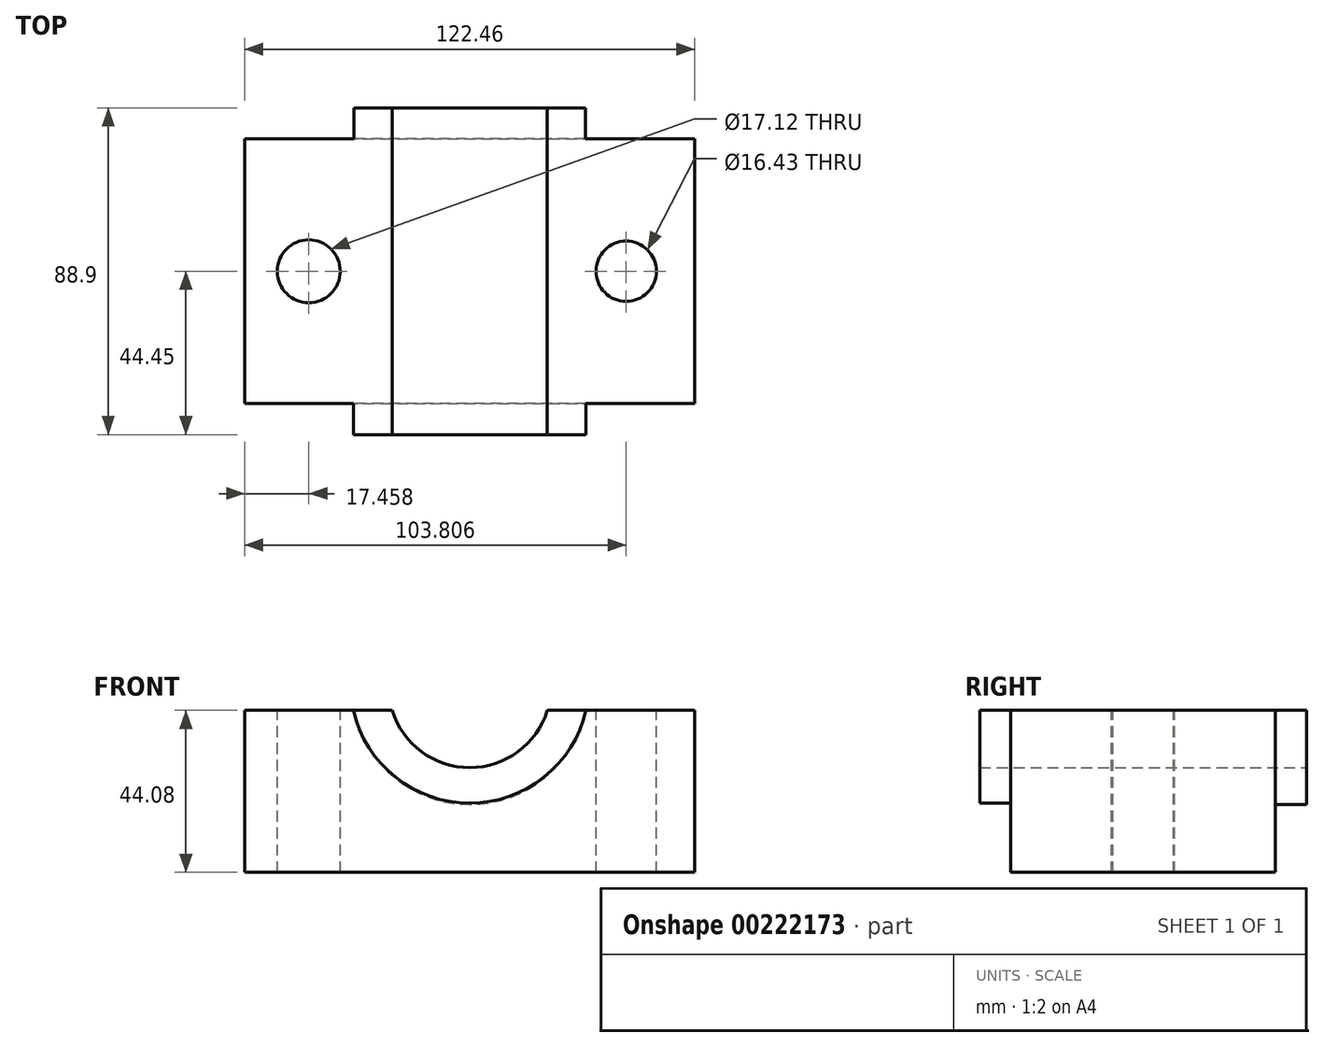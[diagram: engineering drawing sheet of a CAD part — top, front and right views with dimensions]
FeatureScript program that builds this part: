
annotation { "Feature Type Name" : "Feature", "Feature Type Description" : "" }
export const myFeature = defineFeature(function(context is Context, id is Id, definition is map)
    precondition{}
    {
        {
            var Q0;
            Q0=qCreatedBy(makeId("Top.planeOp"),FACE);
            var sketch = newSketch(context, id + "F0", { "sketchPlane" : qUnion([Q0])});
            skLineSegment(sketch, "E0.bottom", {"start": v(-61.23, -36) * mm, "end": v(61.23, -36) * mm});
            skLineSegment(sketch, "E0.top", {"start": v(-61.23, 36) * mm, "end": v(61.23, 36) * mm});
            skLineSegment(sketch, "E0.left", {"start": v(-61.23, -36) * mm, "end": v(-61.23, 36) * mm});
            skLineSegment(sketch, "E0.right", {"start": v(61.23, -36) * mm, "end": v(61.23, 36) * mm});
            skPoint(sketch, "E0.middle", {"position": v(0, 0) * mm});
            skSolve(sketch);
        }
        {
            var Q0;
            Q0 = qSketchRegion(id + "F0", true);
            extrude(context, id + "F1", {"entities" : qUnion([Q0]), "depth" : 76.2 * mm});
        }
        {
            var Q0;
            Q0=qCreatedBy(makeId("Front.planeOp"),FACE);
            var sketch = newSketch(context, id + "F2", { "sketchPlane" : qUnion([Q0])});
            skCircle(sketch, "E1", {"center": v(0, 51.3) * mm, "radius": 32.46 * mm});
            skSolve(sketch);
        }
        {
            var Q0;
            Q0 = qSketchRegion(id + "F2", true);
            extrude(context, id + "F3", {"entities" : qUnion([Q0]), "operationType" : NewBodyOperationType.ADD, "depth" : 44.45 * mm});
        }
        {
            var Q0;
            Q0=qCreatedBy(makeId("Front.planeOp"),FACE);
            var sketch = newSketch(context, id + "F4", { "sketchPlane" : qUnion([Q0])});
            skCircle(sketch, "E2", {"center": v(0, 50.6) * mm, "radius": 32.16 * mm});
            skSolve(sketch);
        }
        {
            var Q0;
            Q0 = qSketchRegion(id + "F4", true);
            extrude(context, id + "F5", {"entities" : qUnion([Q0]), "operationType" : NewBodyOperationType.ADD, "oppositeDirection" : true, "depth" : 44.45 * mm});
        }
        {
            var Q0;
            Q0=makeQuery(id+"F5.opExtrude","CAP_FACE",FACE,{"disambiguationData":[OSD([sQuery(id+"F4.wireOp",EDGE,"E2")])],"isStart":false});
            var sketch = newSketch(context, id + "F6", { "sketchPlane" : qUnion([Q0])});
            skCircle(sketch, "E3", {"center": v(0, 50.6) * mm, "radius": 22.1 * mm});
            skSolve(sketch);
        }
        {
            var Q0;
            Q0 = qSketchRegion(id + "F6", true);
            extrude(context, id + "F7", {"entities" : qUnion([Q0]), "operationType" : NewBodyOperationType.REMOVE, "endBound" : BoundingType.THROUGH_ALL, "oppositeDirection" : true, "depth" : 25.4 * mm});
        }
        {
            var Q0;
            {var subQ0=sQuery(id+"F0.wireOp",EDGE,"E0.left");var subQ2=sQuery(id+"F0.wireOp",EDGE,"E0.top");var subQ3=sQuery(id+"F0.wireOp",EDGE,"E0.bottom");Q0=makeQuery(id+"F5.boolean.opBoolean","SPLIT",FACE,{"disambiguationData":[TD([makeQuery(id+"F1.opExtrude","SWEPT_FACE",FACE,{"disambiguationData":[OSD([subQ0])]})])],"derivedFrom":makeQuery(id+"F1.opExtrude","CAP_FACE",FACE,{"disambiguationData":[OSD([subQ3,subQ2,subQ0,sQuery(id+"F0.wireOp",EDGE,"E0.right")])],"isStart":false})});}
            var sketch = newSketch(context, id + "F8", { "sketchPlane" : qUnion([Q0])});
            skCircle(sketch, "E4", {"center": v(-43.77, 0) * mm, "radius": 8.56 * mm});
            skCircle(sketch, "E5", {"center": v(42.58, 0) * mm, "radius": 8.21 * mm});
            skSolve(sketch);
        }
        {
            var Q0;
            Q0 = qSketchRegion(id + "F8", true);
            extrude(context, id + "F9", {"entities" : qUnion([Q0]), "operationType" : NewBodyOperationType.REMOVE, "endBound" : BoundingType.THROUGH_ALL, "oppositeDirection" : true, "depth" : 25.4 * mm});
        }
        {
            var Q0;
            Q0=makeQuery(id+"F1.opExtrude","SWEPT_FACE",FACE,{"disambiguationData":[OSD([sQuery(id+"F0.wireOp",EDGE,"E0.bottom")])]});
            var sketch = newSketch(context, id + "F10", { "sketchPlane" : qUnion([Q0])});
            skLineSegment(sketch, "E6.bottom", {"start": v(-61.23, 44.08) * mm, "end": v(61.23, 44.08) * mm});
            skLineSegment(sketch, "E6.top", {"start": v(-61.23, 84.5) * mm, "end": v(61.23, 84.5) * mm});
            skLineSegment(sketch, "E6.left", {"start": v(-61.23, 44.08) * mm, "end": v(-61.23, 84.5) * mm});
            skLineSegment(sketch, "E6.right", {"start": v(61.23, 44.08) * mm, "end": v(61.23, 84.5) * mm});
            skSolve(sketch);
        }
        {
            var Q0;
            Q0 = qSketchRegion(id + "F10", true);
            extrude(context, id + "F11", {"entities" : qUnion([Q0]), "operationType" : NewBodyOperationType.REMOVE, "endBound" : BoundingType.THROUGH_ALL, "oppositeDirection" : true, "depth" : 25.4 * mm});
        }
        {
            var Q0;
            Q0=makeQuery(id+"F1.opExtrude","SWEPT_FACE",FACE,{"disambiguationData":[OSD([sQuery(id+"F0.wireOp",EDGE,"E0.bottom")])]});
            var sketch = newSketch(context, id + "F12", { "sketchPlane" : qUnion([Q0])});
            skLineSegment(sketch, "E7.bottom", {"start": v(-61.23, 44.08) * mm, "end": v(61.53, 44.08) * mm});
            skLineSegment(sketch, "E7.top", {"start": v(-61.23, 85.34) * mm, "end": v(61.53, 85.34) * mm});
            skLineSegment(sketch, "E7.left", {"start": v(-61.23, 44.08) * mm, "end": v(-61.23, 85.34) * mm});
            skLineSegment(sketch, "E7.right", {"start": v(61.53, 44.08) * mm, "end": v(61.53, 85.34) * mm});
            skSolve(sketch);
        }
        {
            var Q0;
            Q0 = qSketchRegion(id + "F12", true);
            extrude(context, id + "F13", {"entities" : qUnion([Q0]), "operationType" : NewBodyOperationType.REMOVE, "endBound" : BoundingType.THROUGH_ALL, "oppositeDirection" : true, "depth" : 50.8 * mm});
        }
        {
            var Q0;
            Q0=makeQuery(id+"F11.boolean.opBoolean","COPY",FACE,{"derivedFrom":makeQuery(id+"F11.opExtrude","CAP_FACE",FACE,{"disambiguationData":[OSD([sQuery(id+"F10.wireOp",EDGE,"E6.bottom"),sQuery(id+"F10.wireOp",EDGE,"E6.top"),sQuery(id+"F10.wireOp",EDGE,"E6.left"),sQuery(id+"F10.wireOp",EDGE,"E6.right")])],"isStart":true})});
            var sketch = newSketch(context, id + "F14", { "sketchPlane" : qUnion([Q0])});
            skArc(sketch, "E8", {"start": v(31.65, 44.08) * mm, "mid": v(0, 84.2) * mm, "end": v(-31.65, 44.08) * mm});
            skLineSegment(sketch, "E9", {"start": v(-31.65, 44.08) * mm, "end": v(31.65, 44.08) * mm});
            skSolve(sketch);
        }
        {
            var Q0;
            Q0 = qSketchRegion(id + "F14", true);
            extrude(context, id + "F15", {"entities" : qUnion([Q0]), "operationType" : NewBodyOperationType.REMOVE, "endBound" : BoundingType.THROUGH_ALL, "oppositeDirection" : true, "depth" : 25.4 * mm});
        }
    });
